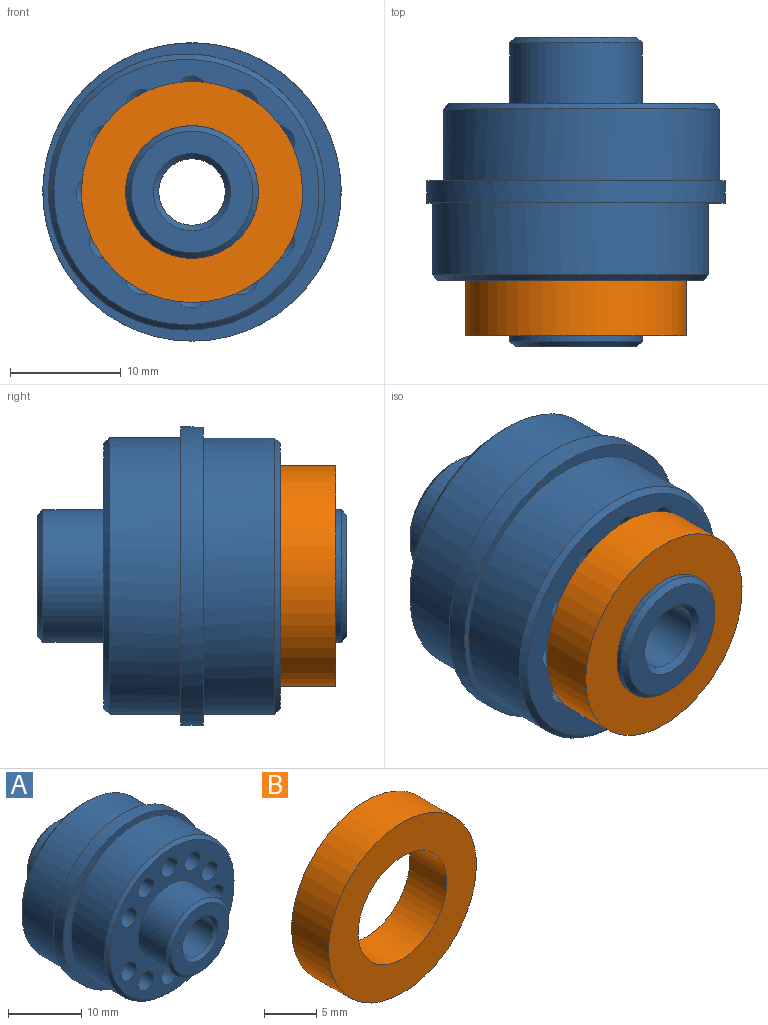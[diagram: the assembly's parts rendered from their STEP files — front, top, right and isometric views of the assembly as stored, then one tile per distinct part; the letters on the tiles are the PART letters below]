
ASSEMBLY  parts=2 mates=1
PART A: 62 faces, bbox 27x28x27 mm
  f0: cylinder r=12.5mm len=25mm, axis (0,1,0), area 510.5mm2, adj f4,f36
  f1: plane 24x24mm, normal (0,-1,0), area 261.5mm2, adj f3,f12,f14,f16,f18,f20,f22,f24
  f2: plane 11x11mm, normal (0,-1,0), area 56.5mm2, adj f37,f39
  f3: cylinder r=6mm len=12mm, axis (0,-1,0), area 207.3mm2, adj f1,f37
  f4: plane 27x27mm, normal (0,-1,0), area 81.7mm2, adj f0,f5
  f5: cylinder r=13.5mm len=27mm, axis (0,1,0), area 169.6mm2, adj f4,f6
  f6: plane 27x27mm, normal (0,1,0), area 81.7mm2, adj f5,f10
  f7: plane 11x11mm, normal (0,1,0), area 56.5mm2, adj f34,f38
  f8: cylinder r=6mm len=12mm, axis (0,-1,0), area 207.3mm2, adj f9,f34
  f9: plane 24x24mm, normal (0,1,0), area 261.5mm2, adj f8,f35,f40,f42,f44,f46,f48,f50
  f10: cylinder r=12.5mm len=25mm, axis (0,-1,0), area 510.5mm2, adj f6,f35
  f11: cylinder r=3mm len=27mm, axis (0,-1,0), area 508.9mm2, adj f38,f39
  f12: cylinder r=1.5mm len=6mm, axis (0,-1,0), area 56.5mm2, adj f1,f13
  f13: cone r=0mm half-angle=59deg, axis (0,-1,0), area 8.2mm2, adj f12
  f14: cylinder r=1.5mm len=6mm, axis (0,-1,0), area 56.5mm2, adj f1,f15
  f15: cone r=0mm half-angle=59deg, axis (0,-1,0), area 8.2mm2, adj f14
  f16: cylinder r=1.5mm len=6mm, axis (0,-1,0), area 56.5mm2, adj f1,f17
  f17: cone r=0mm half-angle=59deg, axis (0,-1,0), area 8.2mm2, adj f16
  f18: cylinder r=1.5mm len=6mm, axis (0,-1,0), area 56.5mm2, adj f1,f19
  f19: cone r=0mm half-angle=59deg, axis (0,-1,0), area 8.2mm2, adj f18
  f20: cylinder r=1.5mm len=6mm, axis (0,-1,0), area 56.5mm2, adj f1,f21
  f21: cone r=0mm half-angle=59deg, axis (0,-1,0), area 8.2mm2, adj f20
  f22: cylinder r=1.5mm len=6mm, axis (0,-1,0), area 56.5mm2, adj f1,f23
  f23: cone r=0mm half-angle=59deg, axis (0,-1,0), area 8.2mm2, adj f22
  f24: cylinder r=1.5mm len=6mm, axis (0,-1,0), area 56.5mm2, adj f1,f25
  f25: cone r=0mm half-angle=59deg, axis (0,-1,0), area 8.2mm2, adj f24
  f26: cylinder r=1.5mm len=6mm, axis (0,-1,0), area 56.5mm2, adj f1,f27
  f27: cone r=0mm half-angle=59deg, axis (0,-1,0), area 8.2mm2, adj f26
  f28: cylinder r=1.5mm len=6mm, axis (0,-1,0), area 56.5mm2, adj f1,f29
  f29: cone r=0mm half-angle=59deg, axis (0,-1,0), area 8.2mm2, adj f28
  f30: cylinder r=1.5mm len=6mm, axis (0,-1,0), area 56.5mm2, adj f1,f31
  f31: cone r=0mm half-angle=59deg, axis (0,-1,0), area 8.2mm2, adj f30
  f32: cylinder r=1.5mm len=6mm, axis (0,-1,0), area 56.5mm2, adj f1,f33
  f33: cone r=0mm half-angle=59deg, axis (0,-1,0), area 8.2mm2, adj f32
  f34: cone r=6mm half-angle=45deg, axis (0,-1,0), area 25.5mm2, adj f7,f8
  f35: cone r=12mm half-angle=45deg, axis (0,-1,0), area 54.4mm2, adj f9,f10
  f36: cone r=12mm half-angle=45deg, axis (0,1,0), area 54.4mm2, adj f0,f1
  f37: cone r=5.5mm half-angle=45deg, axis (0,1,0), area 25.5mm2, adj f2,f3
  f38: cone r=3.5mm half-angle=45deg, axis (0,1,0), area 14.4mm2, adj f7,f11
  f39: cone r=3mm half-angle=45deg, axis (0,-1,0), area 14.4mm2, adj f2,f11
  f40: cylinder r=1.5mm len=6mm, axis (0,1,0), area 56.5mm2, adj f9,f41
  f41: cone r=0mm half-angle=59deg, axis (0,1,0), area 8.2mm2, adj f40
  f42: cylinder r=1.5mm len=6mm, axis (0,1,0), area 56.5mm2, adj f9,f43
  f43: cone r=0mm half-angle=59deg, axis (0,1,0), area 8.2mm2, adj f42
  f44: cylinder r=1.5mm len=6mm, axis (0,1,0), area 56.5mm2, adj f9,f45
  f45: cone r=0mm half-angle=59deg, axis (0,1,0), area 8.2mm2, adj f44
  f46: cylinder r=1.5mm len=6mm, axis (0,1,0), area 56.5mm2, adj f9,f47
  f47: cone r=0mm half-angle=59deg, axis (0,1,0), area 8.2mm2, adj f46
  f48: cylinder r=1.5mm len=6mm, axis (0,1,0), area 56.5mm2, adj f9,f49
  f49: cone r=0mm half-angle=59deg, axis (0,1,0), area 8.2mm2, adj f48
  f50: cylinder r=1.5mm len=6mm, axis (0,1,0), area 56.5mm2, adj f9,f51
  f51: cone r=0mm half-angle=59deg, axis (0,1,0), area 8.2mm2, adj f50
  f52: cylinder r=1.5mm len=6mm, axis (0,1,0), area 56.5mm2, adj f9,f53
  f53: cone r=0mm half-angle=59deg, axis (0,1,0), area 8.2mm2, adj f52
  f54: cylinder r=1.5mm len=6mm, axis (0,1,0), area 56.5mm2, adj f9,f55
  f55: cone r=0mm half-angle=59deg, axis (0,1,0), area 8.2mm2, adj f54
  f56: cylinder r=1.5mm len=6mm, axis (0,1,0), area 56.5mm2, adj f9,f57
  f57: cone r=0mm half-angle=59deg, axis (0,1,0), area 8.2mm2, adj f56
  f58: cylinder r=1.5mm len=6mm, axis (0,1,0), area 56.5mm2, adj f9,f59
  f59: cone r=0mm half-angle=59deg, axis (0,1,0), area 8.2mm2, adj f58
  f60: cylinder r=1.5mm len=6mm, axis (0,1,0), area 56.5mm2, adj f9,f61
  f61: cone r=0mm half-angle=59deg, axis (0,1,0), area 8.2mm2, adj f60
PART B: 4 faces, bbox 20x5x20 mm
  f0: cylinder r=6mm len=12mm, axis (0,-1,0), area 188.5mm2, adj f2,f3
  f1: cylinder r=10mm len=20mm, axis (0,-1,0), area 314.2mm2, adj f2,f3
  f2: plane 20x20mm, normal (0,1,0), area 201.1mm2, adj f0,f1
  f3: plane 20x20mm, normal (0,-1,0), area 201.1mm2, adj f0,f1
PLACE A rot(axis=(1,0,0),180deg) t=(0,-3,0)mm
PLACE B rot(axis=(1,0,0),180deg) t=(0,3,0)mm
MATE fastened B.f0 <-> A.f3  axis (0,1,0) through (0,-11,0)mm
